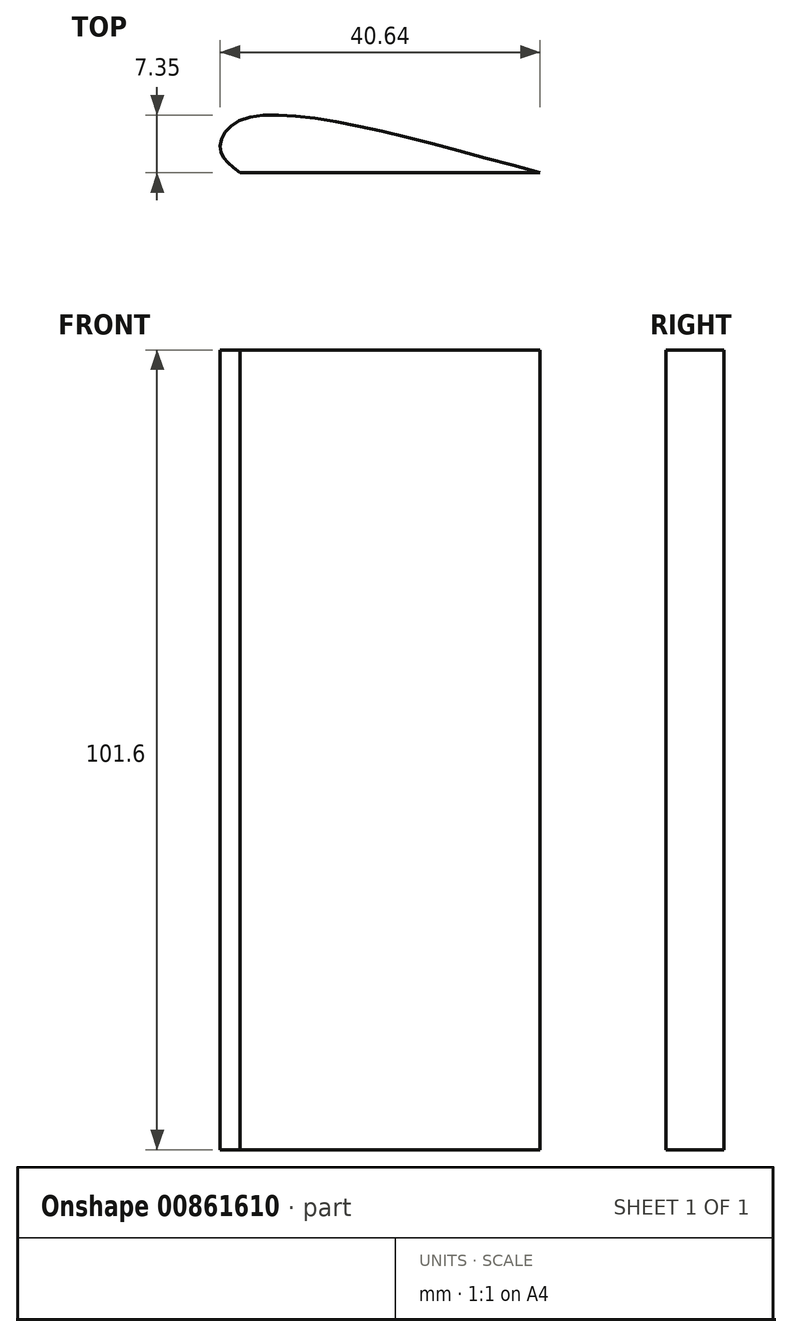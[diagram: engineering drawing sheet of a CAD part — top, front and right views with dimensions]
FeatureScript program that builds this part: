
annotation { "Feature Type Name" : "Feature", "Feature Type Description" : "" }
export const myFeature = defineFeature(function(context is Context, id is Id, definition is map)
    precondition{}
    {
        {
            var Q0;
            Q0=qCreatedBy(makeId("Top.planeOp"),FACE);
            var sketch = newSketch(context, id + "F0", { "sketchPlane" : qUnion([Q0])});
            skLineSegment(sketch, "E0", {"start": v(-17.43, 0) * mm, "end": v(20.67, 0) * mm});
            skFitSpline(sketch, "E1", {"points": [v(-17.43, 0) * mm, v(-19.93, 2.9) * mm, v(-17.43, 6.67) * mm, v(20.67, 0) * mm], "startDerivative": vector(-20.7, 16.12) * mm, "endDerivative": vector(80.18, -21.7) * mm});
            skSolve(sketch);
        }
        {
            var Q0;
            Q0 = qSketchRegion(id + "F0", true);
            extrude(context, id + "F1", {"entities" : qUnion([Q0]), "depth" : 101.6 * mm, "offsetDistance" : 25.4 * mm});
        }
    });
